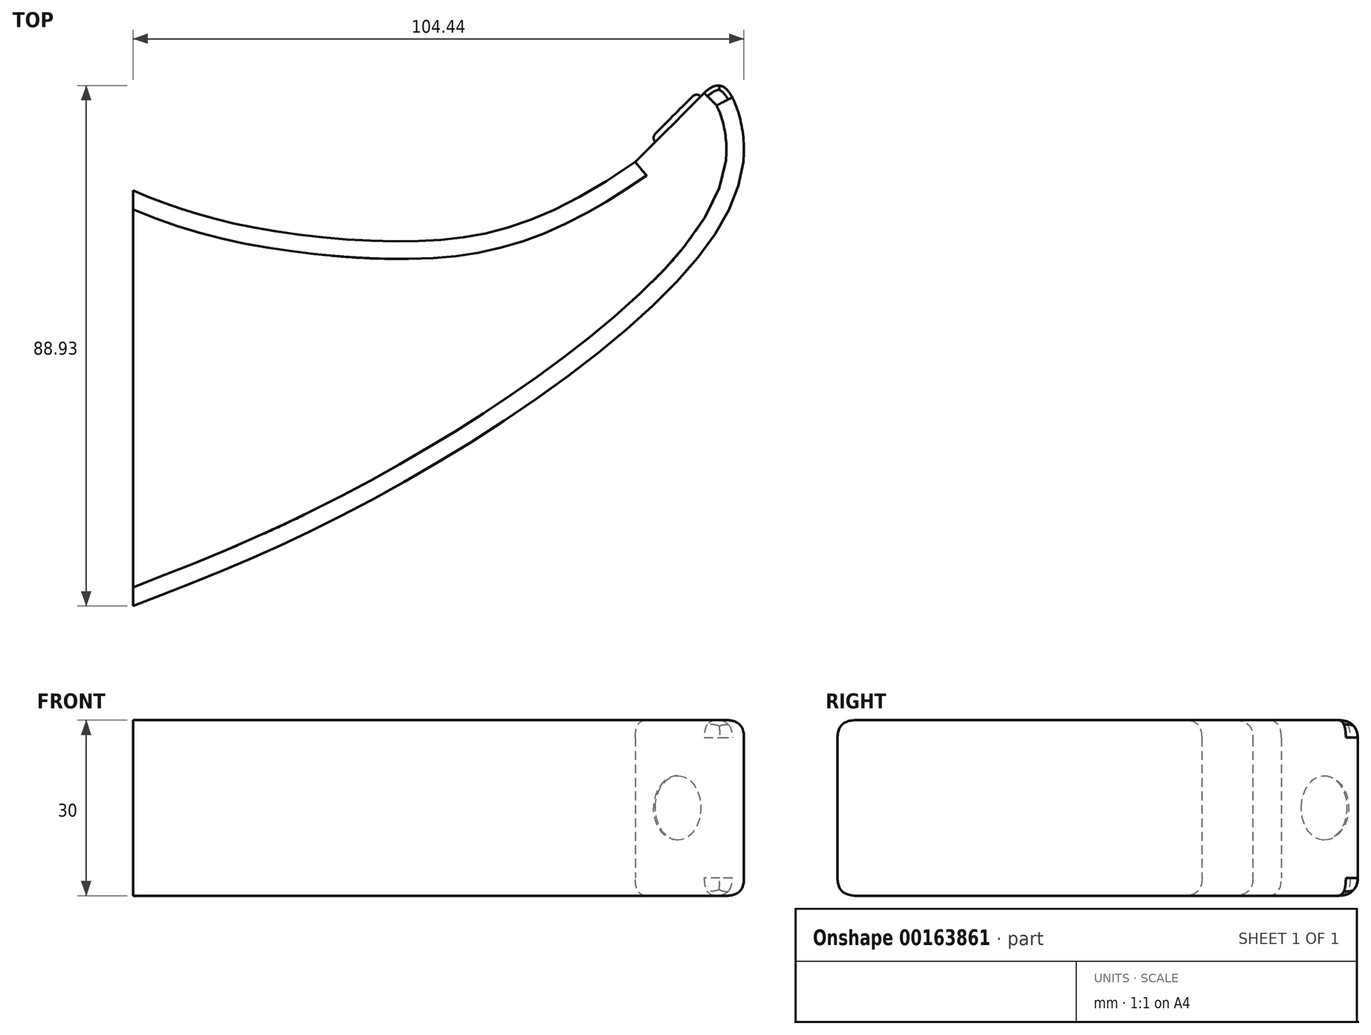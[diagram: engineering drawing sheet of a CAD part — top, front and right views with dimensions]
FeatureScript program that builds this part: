
annotation { "Feature Type Name" : "Feature", "Feature Type Description" : "" }
export const myFeature = defineFeature(function(context is Context, id is Id, definition is map)
    precondition{}
    {
        {
            var Q0;
            Q0=qCreatedBy(makeId("Top.planeOp"),FACE);
            var sketch = newSketch(context, id + "F0", { "sketchPlane" : qUnion([Q0])});
            skLineSegment(sketch, "E0", {"start": v(20.08, 24.8) * mm, "end": v(34.22, 38.94) * mm});
            skLineSegment(sketch, "E1", {"start": v(20.08, 24.8) * mm, "end": v(38.55, 24.8) * mm});
            skLineSegment(sketch, "E2", {"start": v(-65.78, -51.06) * mm, "end": v(-65.78, 48.94) * mm});
            skLineSegment(sketch, "E3", {"start": v(-65.78, -26.25) * mm, "end": v(-65.78, 19.94) * mm});
            skFitSpline(sketch, "E4", {"points": [v(-65.78, 19.94) * mm, v(-48.1, 14.22) * mm, v(-16.48, 11.31) * mm, v(20.08, 24.8) * mm], "startDerivative": vector(62.46, -26.54) * mm, "endDerivative": vector(118.27, 81.8) * mm});
            skFitSpline(sketch, "E5", {"points": [v(-65.78, -51.06) * mm, v(-27.67, -34.37) * mm, v(20.08, -2.5) * mm, v(38.55, 24.8) * mm, v(34.22, 38.94) * mm], "startDerivative": vector(142.55, 54.06) * mm, "endDerivative": vector(-50.17, 36.42) * mm});
            skLineSegment(sketch, "E6", {"start": v(34.22, 38.94) * mm, "end": v(-65.78, 38.94) * mm});
            skSolve(sketch);
        }
        {
            var Q0;
            Q0=sQuery(id+"F0.wireOp",EDGE,"E2");
            extrude(context, id + "F1", {"bodyType" : ToolBodyType.SURFACE, "surfaceEntities" : qUnion([Q0]), "endBound" : BoundingType.SYMMETRIC, "depth" : 100 * mm});
        }
        {
            var Q0;
            {var subQ4=sQuery(id+"F0.wireOp",EDGE,"E1");Q0=makeQuery(id+"F0.imprint","IMPRINT",FACE,{"disambiguationData":[TD([[makeQuery(id+"F0.imprint","IMPRINT",EDGE,{"derivedFrom":subQ4}),-1.0]])]});}
            var Q1;
            {var subQ0=sQuery(id+"F0.wireOp",EDGE,"E0");Q1=makeQuery(id+"F0.imprint","IMPRINT",FACE,{"disambiguationData":[TD([[makeQuery(id+"F0.imprint","IMPRINT",EDGE,{"derivedFrom":subQ0}),-1.0]])]});}
            extrude(context, id + "F2", {"entities" : qUnion([Q0, Q1]), "endBound" : BoundingType.SYMMETRIC, "depth" : 30 * mm});
        }
        {
            var Q0;
            Q0=makeQuery(id+"F2.opExtrude","SWEPT_FACE",FACE,{"disambiguationData":[OSD([sQuery(id+"F0.wireOp",EDGE,"E0")])]});
            var sketch = newSketch(context, id + "F3", { "sketchPlane" : qUnion([Q0])});
            skCircle(sketch, "E7", {"center": v(-42.08, 0) * mm, "radius": 5.5 * mm});
            skSolve(sketch);
        }
        {
            var Q0;
            Q0=makeQuery(id+"F3.imprint","IMPRINT",FACE,{"disambiguationData":[TD([[makeQuery(id+"F3.imprint","IMPRINT",EDGE,{"derivedFrom":sQuery(id+"F3.wireOp",EDGE,"E7")}),1.0]])]});
            extrude(context, id + "F4", {"entities" : qUnion([Q0]), "operationType" : NewBodyOperationType.ADD, "depth" : 1 * mm});
        }
        {
            var Q0;
            Q0=makeQuery(id+"F4.opExtrude","CAP_FACE",FACE,{"disambiguationData":[OSD([sQuery(id+"F3.wireOp",EDGE,"E7")])],"isStart":false});
            fillet(context, id + "F5", {"entities" : qUnion([Q0]), "radius" : 1 * mm, "tangentPropagation" : true, "allowEdgeOverflow" : false});
        }
        {
            var Q0;
            Q0=makeQuery(id+"F2.opExtrude","SWEPT_EDGE",EDGE,{"disambiguationData":[OSD([sQuery(id+"F0.wireOp",EDGE,"E0"),sQuery(id+"F0.wireOp",EDGE,"E5"),sQuery(id+"F0.wireOp",EDGE,"E6")])]});
            var Q1;
            Q1=makeQuery(id+"F2.opExtrude","CAP_EDGE",EDGE,{"disambiguationData":[OSD([sQuery(id+"F0.wireOp",EDGE,"E5")])],"isStart":true});
            var Q2;
            Q2=makeQuery(id+"F2.opExtrude","CAP_EDGE",EDGE,{"disambiguationData":[OSD([sQuery(id+"F0.wireOp",EDGE,"E0")])],"isStart":true});
            var Q3;
            Q3=makeQuery(id+"F2.opExtrude","CAP_EDGE",EDGE,{"disambiguationData":[OSD([sQuery(id+"F0.wireOp",EDGE,"E4")])],"isStart":true});
            var Q4;
            Q4=makeQuery(id+"F2.opExtrude","CAP_EDGE",EDGE,{"disambiguationData":[OSD([sQuery(id+"F0.wireOp",EDGE,"E4")])],"isStart":false});
            var Q5;
            Q5=makeQuery(id+"F2.opExtrude","CAP_EDGE",EDGE,{"disambiguationData":[OSD([sQuery(id+"F0.wireOp",EDGE,"E5")])],"isStart":false});
            var Q6;
            Q6=makeQuery(id+"F2.opExtrude","CAP_EDGE",EDGE,{"disambiguationData":[OSD([sQuery(id+"F0.wireOp",EDGE,"E0")])],"isStart":false});
            fillet(context, id + "F6", {"entities" : qUnion([Q0, Q1, Q2, Q3, Q4, Q5, Q6]), "radius" : 3 * mm, "tangentPropagation" : true, "rho" : 0.5, "crossSection" : FilletCrossSection.CONIC, "allowEdgeOverflow" : false});
        }
    });
